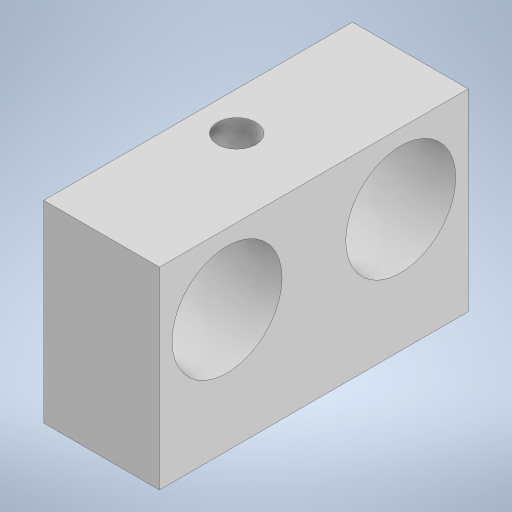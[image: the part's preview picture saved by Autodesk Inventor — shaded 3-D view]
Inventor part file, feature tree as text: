
AUTODESK INVENTOR PART (.ipt)
format: ipt  version: 2024 (Build 280153000, 153)  size: 209,408 bytes
history: native  units: mm
features: sketch x4, extrude x2, sweep x1
ambient origin geometry x8: Origin, YZ Plane, XZ Plane, XY Plane, X Axis, Y Axis, Z Axis, Center Point
bodies: Solid1 (feature_tree)
feature tree (7):
  extrude  "Extrusion1"  Depth=16.0mm
  sweep  "Sweep1"
  extrude  "Extrusion2"  TaperAngle=60.0deg  [1 undecoded]
  sketch  "Sketch1"  dims[d0=6.0mm d1=16.0mm]
  sketch  "Sketch2"  dims[d2=10.0mm d3=0.0mm d4=2.0mm]
  sketch  "Sketch3"  dims[d5=2.0mm d6=60.0deg]
  sketch  "Sketch4"  dims[d7=0.0mm d8=0.0mm d9=5.7mm d10=5.7mm d11=10.0mm d12=0.0mm]
note: 1 required parameter value undecoded (feature->parameter linkage not recoverable at this tier; creation-order binding heuristic only, values carry confidence <= 0.55)
